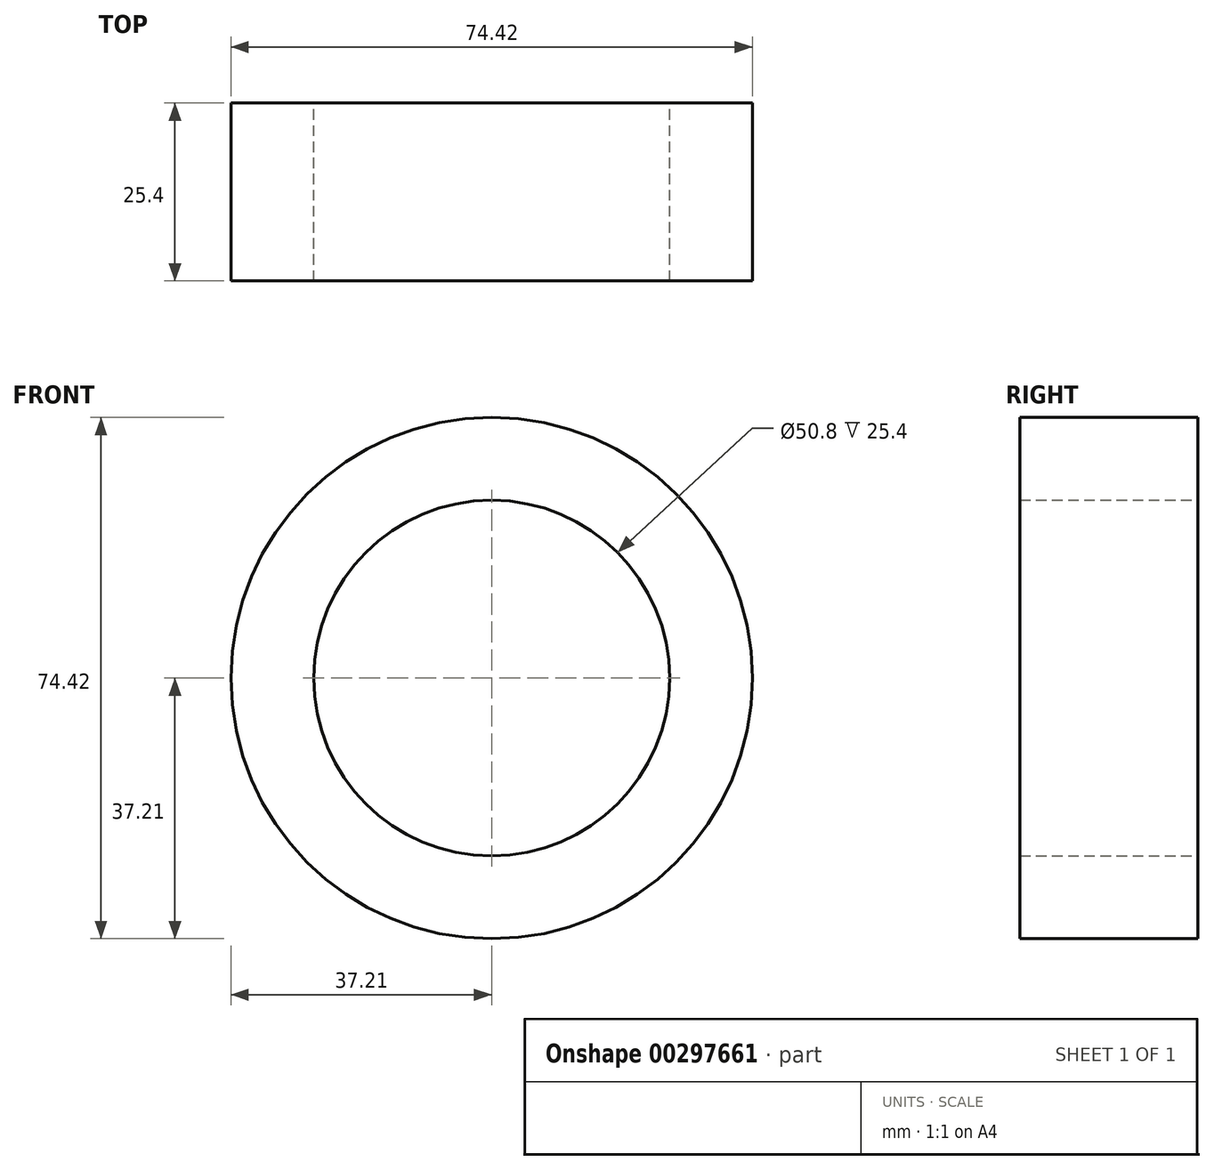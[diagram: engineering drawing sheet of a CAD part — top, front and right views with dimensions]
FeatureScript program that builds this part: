
annotation { "Feature Type Name" : "Feature", "Feature Type Description" : "" }
export const myFeature = defineFeature(function(context is Context, id is Id, definition is map)
    precondition{}
    {
        {
            var Q0;
            Q0=qCreatedBy(makeId("Front.planeOp"),FACE);
            var sketch = newSketch(context, id + "F0", { "sketchPlane" : qUnion([Q0])});
            skCircle(sketch, "E0", {"center": v(0, 0) * mm, "radius": 37.21 * mm});
            skSolve(sketch);
        }
        {
            var Q0;
            Q0=qSketchRegion(id+"F0",true);
            extrude(context, id + "F1", {"entities" : qUnion([Q0]), "depth" : 25.4 * mm});
        }
        {
            var Q0;
            Q0=qCreatedBy(makeId("Front.planeOp"),FACE);
            var sketch = newSketch(context, id + "F2", { "sketchPlane" : qUnion([Q0])});
            skCircle(sketch, "E1", {"center": v(0, 0) * mm, "radius": 28.55 * mm});
            skSolve(sketch);
        }
        {
            var Q0;
            Q0=sQuery(id+"F2.wireOp",VERTEX,"E1.center");
            var Q1;
            Q1=makeQuery(id+"F1.opExtrude","SWEPT_BODY",BODY,{"disambiguationData":[OSD([sQuery(id+"F0.wireOp",EDGE,"E0")])]});
            hole(context, id + "F3", {"style" : HoleStyle.SIMPLE, "endStyle" : HoleEndStyle.THROUGH, "oppositeDirection" : true, "holeDiameter" : 50.8 * mm, "locations" : qUnion([Q0]), "scope" : qUnion([Q1]), "isTappedThrough" : true});
        }
    });
